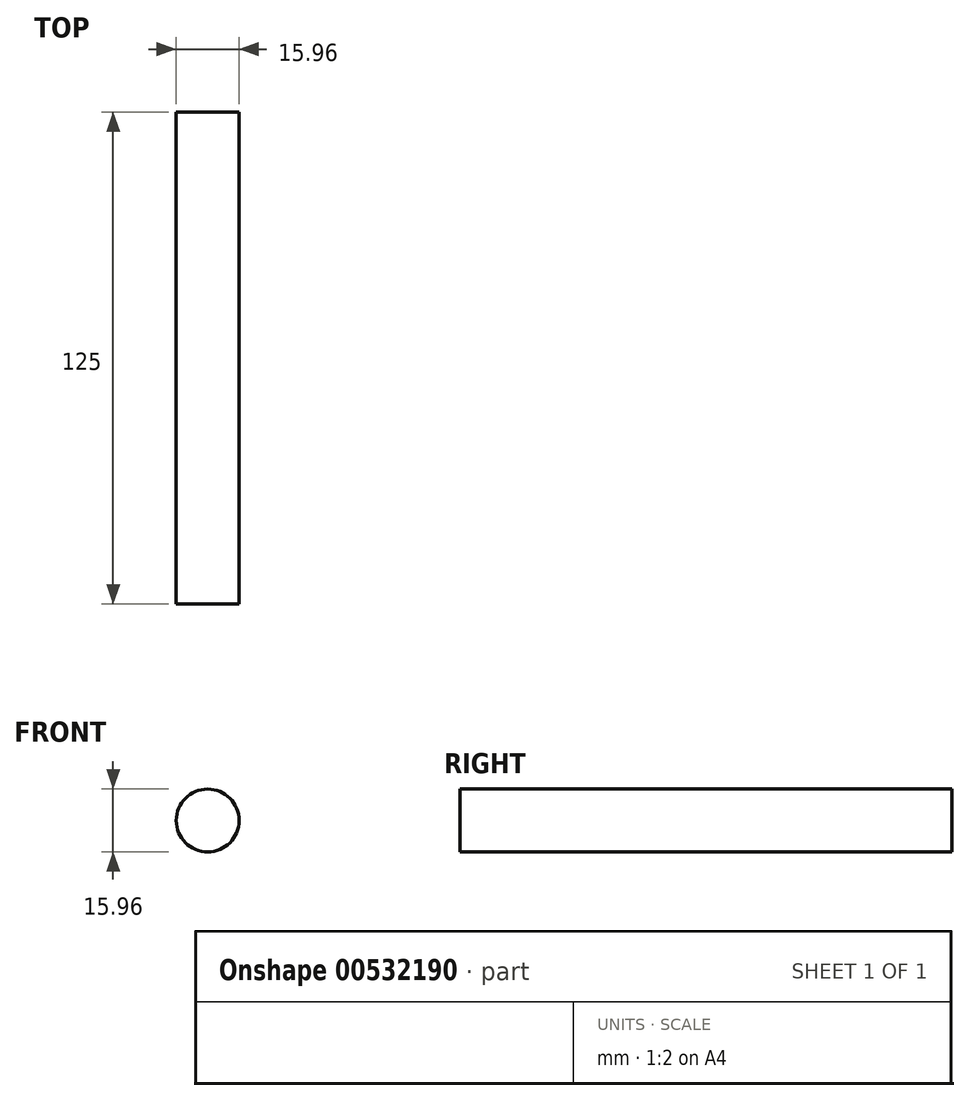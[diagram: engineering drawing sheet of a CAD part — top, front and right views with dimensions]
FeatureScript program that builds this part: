
annotation { "Feature Type Name" : "Feature", "Feature Type Description" : "" }
export const myFeature = defineFeature(function(context is Context, id is Id, definition is map)
    precondition{}
    {
        {
            var Q0;
            Q0=qCreatedBy(makeId("Front.planeOp"),FACE);
            var sketch = newSketch(context, id + "F0", { "sketchPlane" : qUnion([Q0])});
            skCircle(sketch, "E0", {"center": v(0, 0) * mm, "radius": 7.97 * mm});
            skSolve(sketch);
        }
        {
            var Q0;
            Q0=makeQuery(id+"F0.imprint","IMPRINT",FACE,{"disambiguationData":[TD([[makeQuery(id+"F0.imprint","IMPRINT",EDGE,{"derivedFrom":sQuery(id+"F0.wireOp",EDGE,"E0")}),1.0]])]});
            extrude(context, id + "F1", {"entities" : qUnion([Q0]), "oppositeDirection" : true, "depth" : 125 * mm, "offsetDistance" : 25 * mm});
        }
    });
